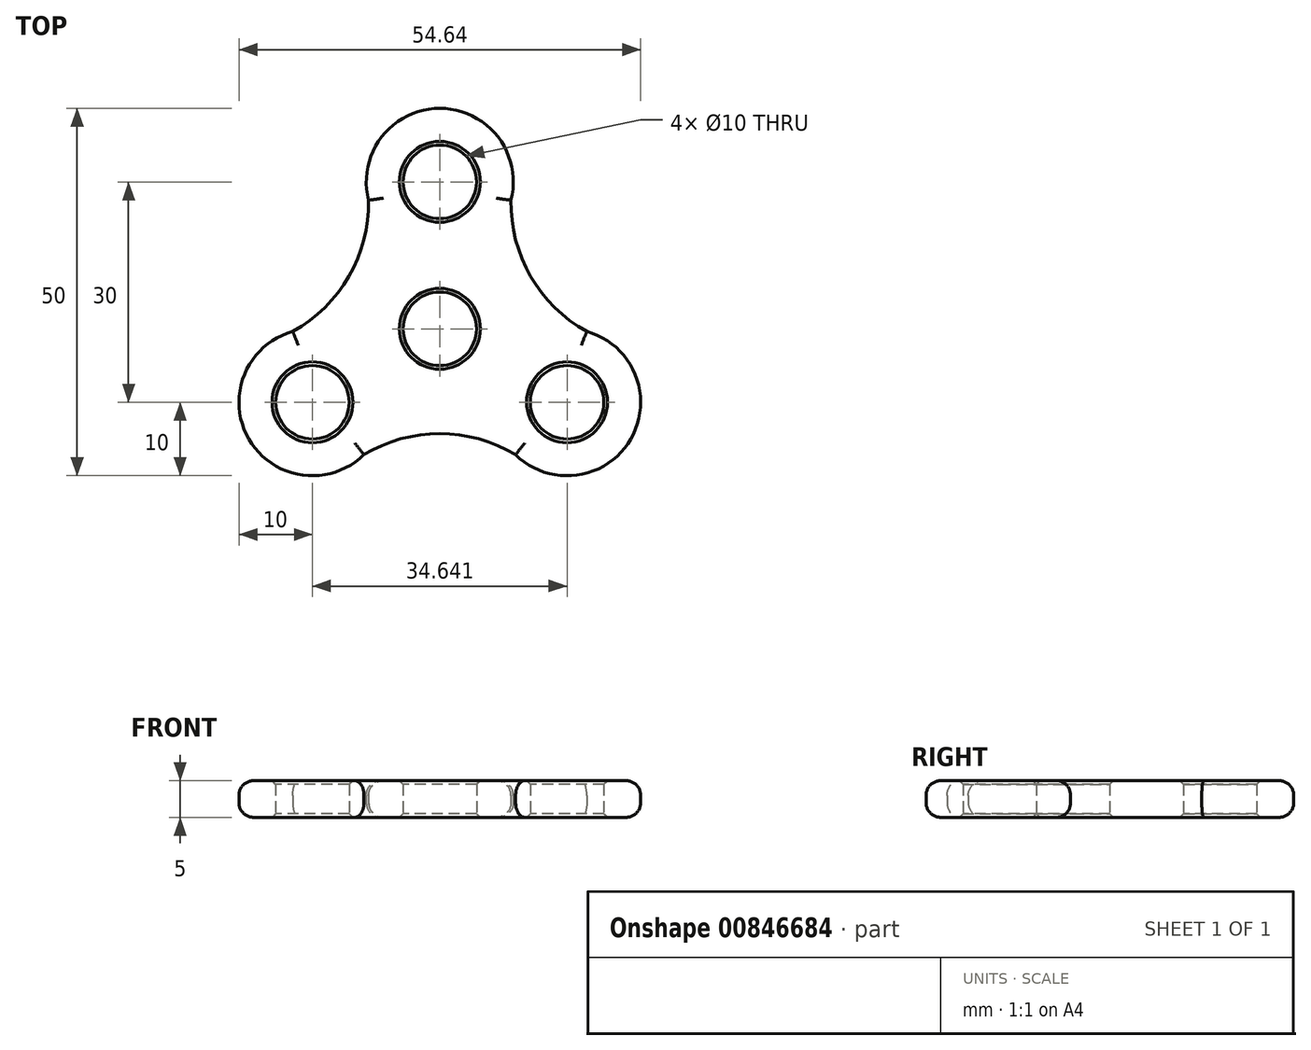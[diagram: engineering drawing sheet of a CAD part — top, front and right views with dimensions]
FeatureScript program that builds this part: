
annotation { "Feature Type Name" : "Feature", "Feature Type Description" : "" }
export const myFeature = defineFeature(function(context is Context, id is Id, definition is map)
    precondition{}
    {
        {
            var Q0;
            Q0=qCreatedBy(makeId("Top.planeOp"),FACE);
            var sketch = newSketch(context, id + "F0", { "sketchPlane" : qUnion([Q0])});
            skArc(sketch, "E0", {"start": v(9.68, 17.5) * mm, "mid": v(0, 30) * mm, "end": v(-9.68, 17.5) * mm});
            skCircle(sketch, "E1", {"center": v(0, 20) * mm, "radius": 5 * mm});
            skArc(sketch, "E2.1.0", {"start": v(-20, -0.36) * mm, "mid": v(-25.98, -15) * mm, "end": v(-10.31, -17.14) * mm});
            skArc(sketch, "E2.2.0", {"start": v(10.31, -17.14) * mm, "mid": v(25.98, -15) * mm, "end": v(20, -0.36) * mm});
            skPoint(sketch, "E2.center", {"position": v(0, 0) * mm});
            skCircle(sketch, "E3", {"center": v(17.32, -10) * mm, "radius": 5 * mm});
            skCircle(sketch, "E4", {"center": v(-17.32, -10) * mm, "radius": 5 * mm});
            skCircle(sketch, "E5", {"center": v(0, 0) * mm, "radius": 5 * mm});
            skArc(sketch, "E6", {"start": v(-20, -0.36) * mm, "mid": v(-12.36, 7.14) * mm, "end": v(-9.68, 17.5) * mm});
            skArc(sketch, "E7", {"start": v(9.68, 17.5) * mm, "mid": v(12.36, 7.14) * mm, "end": v(20, -0.36) * mm});
            skArc(sketch, "E8", {"start": v(10.31, -17.14) * mm, "mid": v(0, -14.27) * mm, "end": v(-10.31, -17.14) * mm});
            skSolve(sketch);
        }
        {
            var Q0;
            Q0 = qSketchRegion(id + "F0", true);
            extrude(context, id + "F1", {"entities" : qUnion([Q0]), "depth" : 5 * mm, "offsetDistance" : 25 * mm});
        }
        {
            var Q0;
            Q0=makeQuery(id+"F1.opExtrude","CAP_EDGE",EDGE,{"disambiguationData":[OSD([sQuery(id+"F0.wireOp",EDGE,"E8")])],"isStart":false});
            var Q1;
            Q1=makeQuery(id+"F1.opExtrude","CAP_EDGE",EDGE,{"disambiguationData":[OSD([sQuery(id+"F0.wireOp",EDGE,"E2.2.0")])],"isStart":false});
            var Q2;
            Q2=makeQuery(id+"F1.opExtrude","CAP_EDGE",EDGE,{"disambiguationData":[OSD([sQuery(id+"F0.wireOp",EDGE,"E7")])],"isStart":false});
            var Q3;
            Q3=makeQuery(id+"F1.opExtrude","CAP_EDGE",EDGE,{"disambiguationData":[OSD([sQuery(id+"F0.wireOp",EDGE,"E0")])],"isStart":false});
            var Q4;
            Q4=makeQuery(id+"F1.opExtrude","CAP_EDGE",EDGE,{"disambiguationData":[OSD([sQuery(id+"F0.wireOp",EDGE,"E6")])],"isStart":false});
            var Q5;
            Q5=makeQuery(id+"F1.opExtrude","CAP_EDGE",EDGE,{"disambiguationData":[OSD([sQuery(id+"F0.wireOp",EDGE,"E2.1.0")])],"isStart":false});
            var Q6;
            Q6=makeQuery(id+"F1.opExtrude","CAP_EDGE",EDGE,{"disambiguationData":[OSD([sQuery(id+"F0.wireOp",EDGE,"E7")])],"isStart":true});
            var Q7;
            Q7=makeQuery(id+"F1.opExtrude","CAP_EDGE",EDGE,{"disambiguationData":[OSD([sQuery(id+"F0.wireOp",EDGE,"E2.2.0")])],"isStart":true});
            var Q8;
            Q8=makeQuery(id+"F1.opExtrude","CAP_EDGE",EDGE,{"disambiguationData":[OSD([sQuery(id+"F0.wireOp",EDGE,"E8")])],"isStart":true});
            var Q9;
            Q9=makeQuery(id+"F1.opExtrude","CAP_EDGE",EDGE,{"disambiguationData":[OSD([sQuery(id+"F0.wireOp",EDGE,"E2.1.0")])],"isStart":true});
            var Q10;
            Q10=makeQuery(id+"F1.opExtrude","CAP_EDGE",EDGE,{"disambiguationData":[OSD([sQuery(id+"F0.wireOp",EDGE,"E6")])],"isStart":true});
            var Q11;
            Q11=makeQuery(id+"F1.opExtrude","CAP_EDGE",EDGE,{"disambiguationData":[OSD([sQuery(id+"F0.wireOp",EDGE,"E0")])],"isStart":true});
            fillet(context, id + "F2", {"entities" : qUnion([Q0, Q1, Q2, Q3, Q4, Q5, Q6, Q7, Q8, Q9, Q10, Q11]), "radius" : 2 * mm, "tangentPropagation" : true, "allowEdgeOverflow" : false});
        }
        {
            var Q0;
            Q0=makeQuery(id+"F1.opExtrude","CAP_EDGE",EDGE,{"disambiguationData":[OSD([sQuery(id+"F0.wireOp",EDGE,"E3")])],"isStart":false});
            var Q1;
            Q1=makeQuery(id+"F1.opExtrude","CAP_EDGE",EDGE,{"disambiguationData":[OSD([sQuery(id+"F0.wireOp",EDGE,"E5")])],"isStart":false});
            var Q2;
            Q2=makeQuery(id+"F1.opExtrude","CAP_EDGE",EDGE,{"disambiguationData":[OSD([sQuery(id+"F0.wireOp",EDGE,"E4")])],"isStart":false});
            var Q3;
            Q3=makeQuery(id+"F1.opExtrude","CAP_EDGE",EDGE,{"disambiguationData":[OSD([sQuery(id+"F0.wireOp",EDGE,"E1")])],"isStart":false});
            var Q4;
            Q4=makeQuery(id+"F1.opExtrude","CAP_EDGE",EDGE,{"disambiguationData":[OSD([sQuery(id+"F0.wireOp",EDGE,"E1")])],"isStart":true});
            var Q5;
            Q5=makeQuery(id+"F1.opExtrude","CAP_EDGE",EDGE,{"disambiguationData":[OSD([sQuery(id+"F0.wireOp",EDGE,"E5")])],"isStart":true});
            var Q6;
            Q6=makeQuery(id+"F1.opExtrude","CAP_EDGE",EDGE,{"disambiguationData":[OSD([sQuery(id+"F0.wireOp",EDGE,"E4")])],"isStart":true});
            var Q7;
            Q7=makeQuery(id+"F1.opExtrude","CAP_EDGE",EDGE,{"disambiguationData":[OSD([sQuery(id+"F0.wireOp",EDGE,"E3")])],"isStart":true});
            chamfer(context, id + "F3", {"entities" : qUnion([Q0, Q1, Q2, Q3, Q4, Q5, Q6, Q7]), "width" : .5 * mm, "tangentPropagation" : true});
        }
    });
